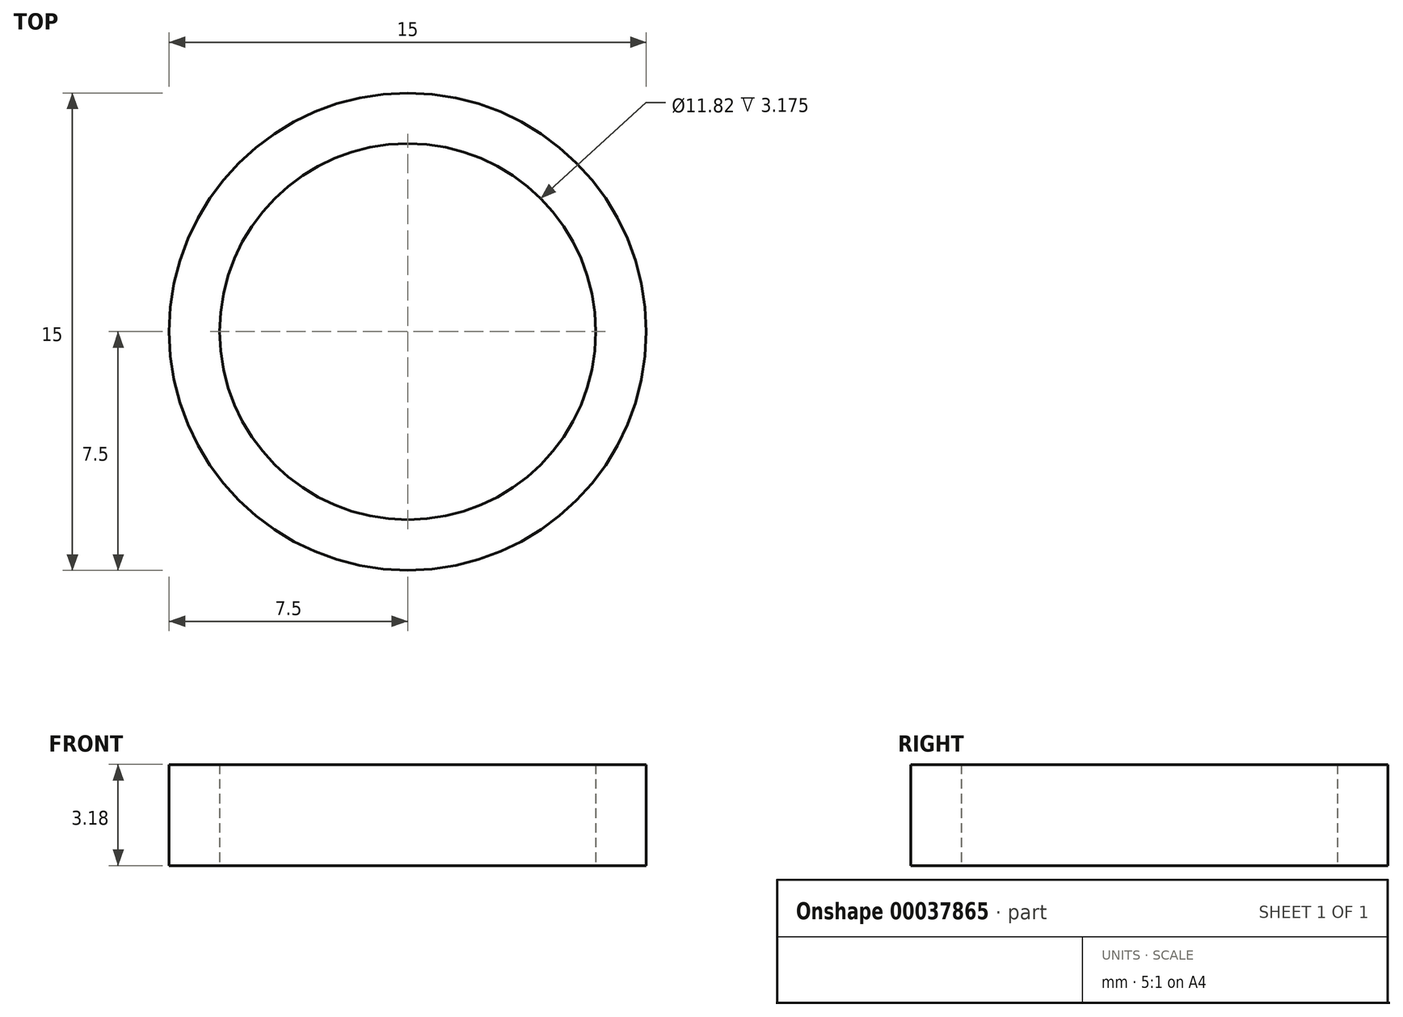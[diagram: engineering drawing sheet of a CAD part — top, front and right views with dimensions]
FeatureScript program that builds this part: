
annotation { "Feature Type Name" : "Feature", "Feature Type Description" : "" }
export const myFeature = defineFeature(function(context is Context, id is Id, definition is map)
    precondition{}
    {
        {
            var Q0;
            Q0=qCreatedBy(makeId("Top.planeOp"),FACE);
            var sketch = newSketch(context, id + "F0", { "sketchPlane" : qUnion([Q0])});
            skCircle(sketch, "E0", {"center": v(0, 0) * mm, "radius": 5.91 * mm});
            skCircle(sketch, "E1", {"center": v(0, 0) * mm, "radius": 7.5 * mm});
            skSolve(sketch);
        }
        {
            var Q0;
            Q0 = qSketchRegion(id + "F0", true);
            extrude(context, id + "F1", {"entities" : qUnion([Q0]), "depth" : 3.17 * mm});
        }
    });
